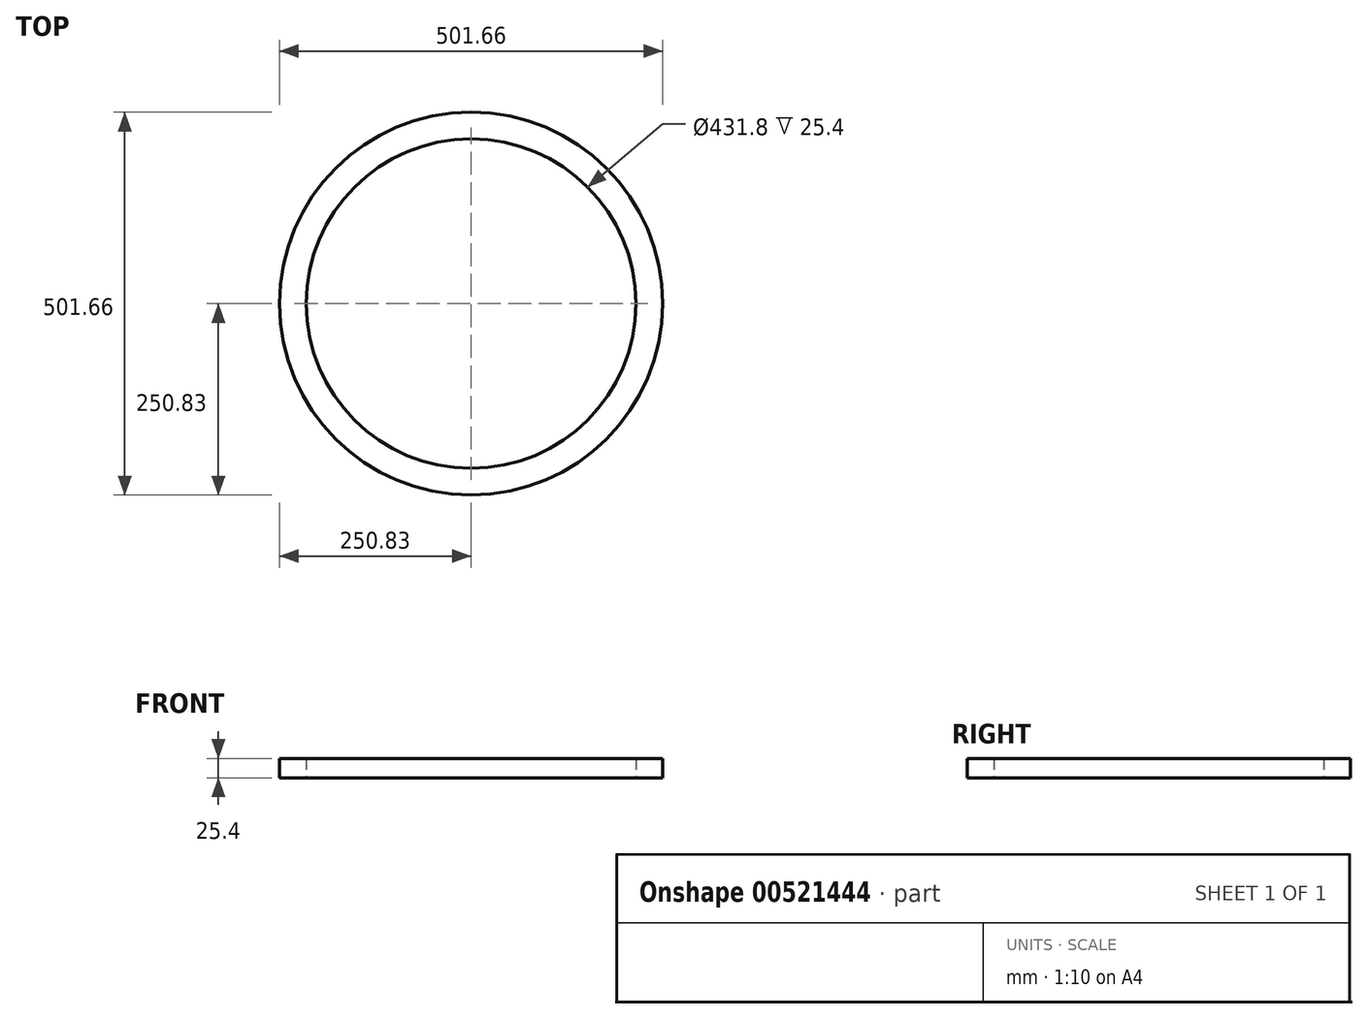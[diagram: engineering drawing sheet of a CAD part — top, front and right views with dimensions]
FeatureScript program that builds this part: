
annotation { "Feature Type Name" : "Feature", "Feature Type Description" : "" }
export const myFeature = defineFeature(function(context is Context, id is Id, definition is map)
    precondition{}
    {
        {
            var Q0;
            Q0=qCreatedBy(makeId("Top.planeOp"),FACE);
            var sketch = newSketch(context, id + "F0", { "sketchPlane" : qUnion([Q0])});
            skCircle(sketch, "E0", {"center": v(0, 0) * mm, "radius": 250.83 * mm});
            skSolve(sketch);
        }
        {
            var Q0;
            Q0=makeQuery(id+"F0.imprint","IMPRINT",FACE,{"disambiguationData":[TD([[makeQuery(id+"F0.imprint","IMPRINT",EDGE,{"derivedFrom":sQuery(id+"F0.wireOp",EDGE,"E0")}),1.0]])]});
            extrude(context, id + "F1", {"entities" : qUnion([Q0]), "depth" : 25.4 * mm, "offsetDistance" : 25.4 * mm});
        }
        {
            var Q0;
            Q0=makeQuery(id+"F1.opExtrude","CAP_FACE",FACE,{"disambiguationData":[OSD([sQuery(id+"F0.wireOp",EDGE,"E0")])],"isStart":true});
            var sketch = newSketch(context, id + "F2", { "sketchPlane" : qUnion([Q0])});
            skPoint(sketch, "E1", {"position": v(0, 0) * mm});
            skSolve(sketch);
        }
        {
            var Q0;
            Q0=sQuery(id+"F2.wireOp",VERTEX,"E1");
            var Q1;
            Q1=makeQuery(id+"F1.opExtrude","SWEPT_BODY",BODY,{"disambiguationData":[OSD([sQuery(id+"F0.wireOp",EDGE,"E0")])]});
            hole(context, id + "F3", {"style" : HoleStyle.SIMPLE, "endStyle" : HoleEndStyle.THROUGH, "holeDiameter" : 431.8 * mm, "isTappedThrough" : true, "tappedDepth" : 12.7 * mm, "tapClearance" : 3, "locations" : qUnion([Q0]), "scope" : qUnion([Q1])});
        }
    });
